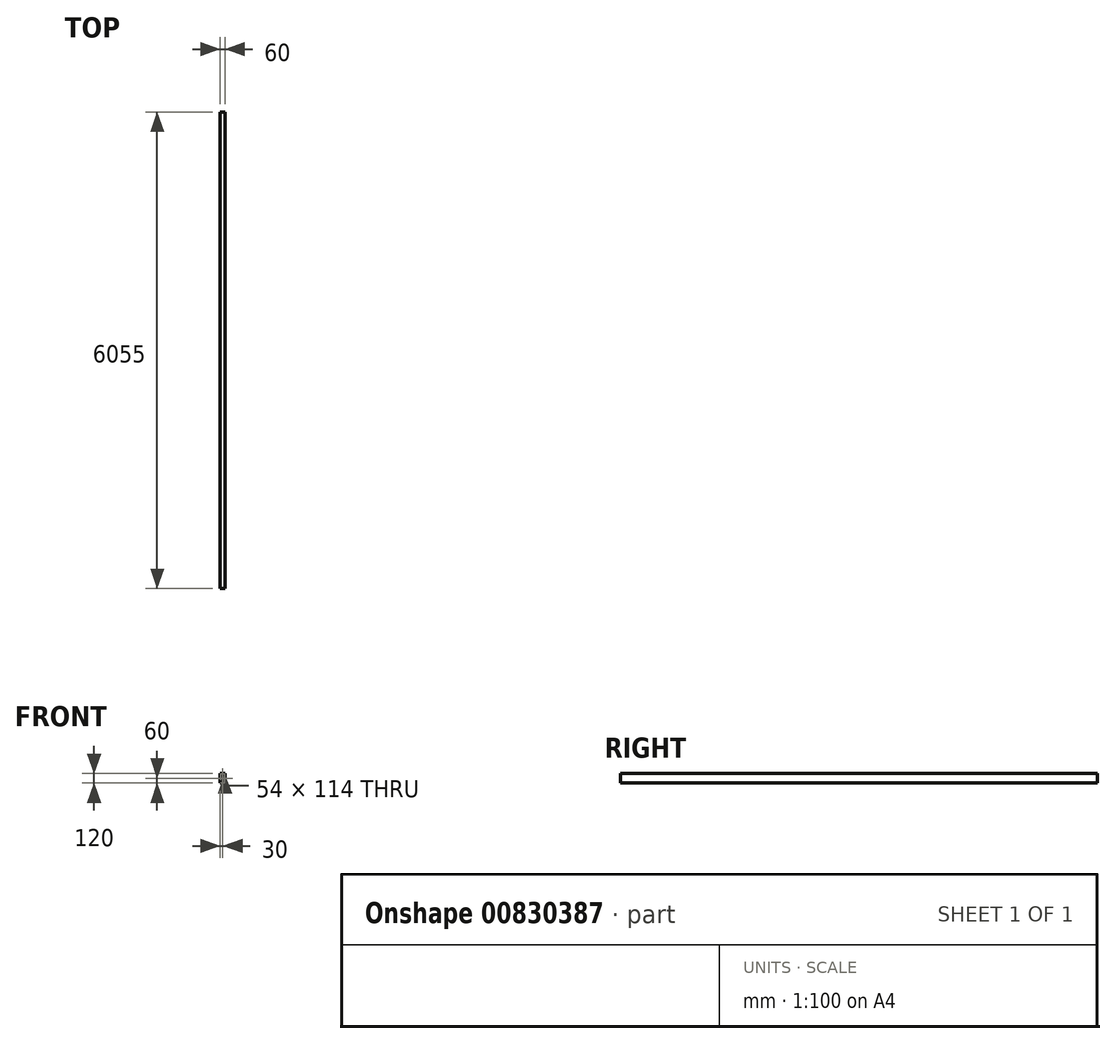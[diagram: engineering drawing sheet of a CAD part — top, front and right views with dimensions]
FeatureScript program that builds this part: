
annotation { "Feature Type Name" : "Feature", "Feature Type Description" : "" }
export const myFeature = defineFeature(function(context is Context, id is Id, definition is map)
    precondition{}
    {
        {
            var Q0;
            Q0=qCreatedBy(makeId("Front.planeOp"),FACE);
            var sketch = newSketch(context, id + "F0", { "sketchPlane" : qUnion([Q0])});
            skLineSegment(sketch, "E0.bottom", {"start": v(30, 60) * mm, "end": v(-30, 60) * mm});
            skLineSegment(sketch, "E0.top", {"start": v(30, -60) * mm, "end": v(-30, -60) * mm});
            skLineSegment(sketch, "E0.left", {"start": v(30, 60) * mm, "end": v(30, -60) * mm});
            skLineSegment(sketch, "E0.right", {"start": v(-30, 60) * mm, "end": v(-30, -60) * mm});
            skPoint(sketch, "E0.middle", {"position": v(0, 0) * mm});
            skLineSegment(sketch, "E1.0", {"start": v(-27, 57) * mm, "end": v(-27, -57) * mm});
            skLineSegment(sketch, "E1.1", {"start": v(27, 57) * mm, "end": v(-27, 57) * mm});
            skLineSegment(sketch, "E1.2", {"start": v(27, 57) * mm, "end": v(27, -57) * mm});
            skLineSegment(sketch, "E1.3", {"start": v(27, -57) * mm, "end": v(-27, -57) * mm});
            skSolve(sketch);
        }
        {
            var Q0;
            Q0=qCreatedBy(makeId("Right.planeOp"),FACE);
            var sketch = newSketch(context, id + "F1", { "sketchPlane" : qUnion([Q0])});
            skLineSegment(sketch, "E2", {"start": v(0, 0) * mm, "end": v(-6055, 0) * mm});
            skSolve(sketch);
        }
        {
            var Q0;
            Q0 = qSketchRegion(id + "F0", true);
            var Q1;
            Q1 = qConstructionFilter(qBodyType(qCreatedBy(id + "F1" ,EDGE), BodyType.WIRE), ConstructionObject.NO);
            sweep(context, id + "F2", {"profiles" : qUnion([Q0]), "path" : qUnion([Q1])});
        }
    });
